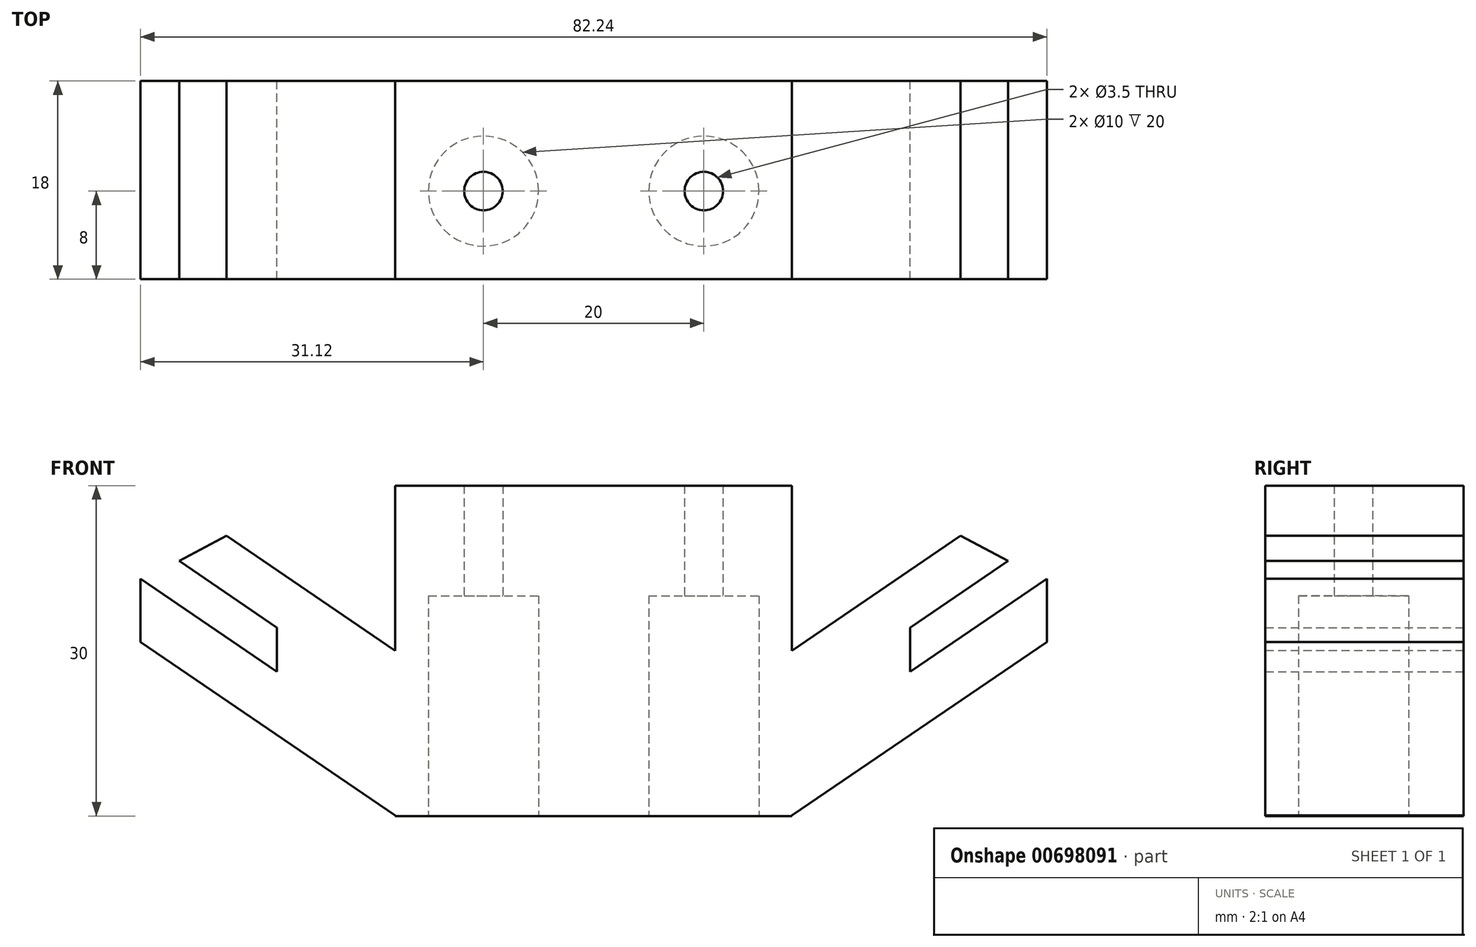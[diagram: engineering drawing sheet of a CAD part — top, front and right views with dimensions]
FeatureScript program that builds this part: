
annotation { "Feature Type Name" : "Feature", "Feature Type Description" : "" }
export const myFeature = defineFeature(function(context is Context, id is Id, definition is map)
    precondition{}
    {
        {
            var Q0;
            Q0=qCreatedBy(makeId("Top.planeOp"),FACE);
            var sketch = newSketch(context, id + "F0", { "sketchPlane" : qUnion([Q0])});
            skLineSegment(sketch, "E0.top", {"start": v(-10, -10) * mm, "end": v(10, -10) * mm, "construction": true});
            skPoint(sketch, "E0.middle", {"position": v(0, 0) * mm});
            skLineSegment(sketch, "E1.1", {"start": v(-18, 0) * mm, "end": v(-18, -18) * mm});
            skLineSegment(sketch, "E1.2", {"start": v(-18, -18) * mm, "end": v(18, -18) * mm});
            skLineSegment(sketch, "E1.3", {"start": v(18, 0) * mm, "end": v(18, -18) * mm});
            skLineSegment(sketch, "E2", {"start": v(-18, 0) * mm, "end": v(18, 0) * mm});
            skPoint(sketch, "E3.orphan", {"position": v(10, 10) * mm});
            skPoint(sketch, "E4.orphan", {"position": v(-10, 10) * mm});
            skPoint(sketch, "E1.0.end.orphan", {"position": v(18, 18) * mm});
            skPoint(sketch, "E1.0.start.orphan", {"position": v(-18, 18) * mm});
            skSolve(sketch);
        }
        {
            var Q0;
            Q0=makeQuery(id+"F0.imprint","IMPRINT",FACE,{"disambiguationData":[TD([[makeQuery(id+"F0.imprint","IMPRINT",EDGE,{"derivedFrom":sQuery(id+"F0.wireOp",EDGE,"E1.1")}),1.0]])]});
            extrude(context, id + "F1", {"entities" : qUnion([Q0]), "depth" : 15 * mm, "offsetDistance" : 25 * mm});
        }
        {
            var Q0;
            Q0=qCreatedBy(makeId("Front.planeOp"),FACE);
            var sketch = newSketch(context, id + "F2", { "sketchPlane" : qUnion([Q0])});
            skLineSegment(sketch, "E5", {"start": v(-18, 15) * mm, "end": v(-41.12, 30.79) * mm});
            skLineSegment(sketch, "E6", {"start": v(-41.12, 30.79) * mm, "end": v(-41.12, 25.56) * mm});
            skLineSegment(sketch, "E7", {"start": v(-41.12, 15.79) * mm, "end": v(-17.94, 0) * mm});
            skLineSegment(sketch, "E8", {"start": v(-41.12, 25.56) * mm, "end": v(-28.74, 17.1) * mm});
            skLineSegment(sketch, "E9", {"start": v(-28.74, 17.1) * mm, "end": v(-28.74, 13.1) * mm});
            skLineSegment(sketch, "E10", {"start": v(-28.74, 13.1) * mm, "end": v(-41.12, 21.56) * mm});
            skLineSegment(sketch, "E11.trimOffspring", {"start": v(-41.12, 21.56) * mm, "end": v(-41.12, 15.79) * mm});
            skLineSegment(sketch, "E12", {"start": v(-18, 15) * mm, "end": v(-17.94, 0) * mm});
            skLineSegment(sketch, "E13.MirrorCS", {"start": v(41.12, 25.56) * mm, "end": v(28.74, 17.1) * mm});
            skLineSegment(sketch, "E14.MirrorCS", {"start": v(28.74, 17.1) * mm, "end": v(28.74, 13.1) * mm});
            skLineSegment(sketch, "E15.MirrorCS", {"start": v(18, 15) * mm, "end": v(41.12, 30.79) * mm});
            skLineSegment(sketch, "E16.MirrorCS", {"start": v(28.74, 13.1) * mm, "end": v(41.12, 21.56) * mm});
            skLineSegment(sketch, "E17.MirrorCS", {"start": v(41.12, 15.79) * mm, "end": v(17.94, 0) * mm});
            skLineSegment(sketch, "E18.MirrorCS", {"start": v(41.12, 21.56) * mm, "end": v(41.12, 15.79) * mm});
            skLineSegment(sketch, "E19.MirrorCS", {"start": v(41.12, 30.79) * mm, "end": v(41.12, 25.56) * mm});
            skLineSegment(sketch, "E20.MirrorCS", {"start": v(18, 15) * mm, "end": v(17.94, 0) * mm});
            skSolve(sketch);
        }
        {
            var Q0;
            Q0=makeQuery(id+"F2.imprint","IMPRINT",FACE,{"disambiguationData":[TD([[makeQuery(id+"F2.imprint","IMPRINT",EDGE,{"derivedFrom":sQuery(id+"F2.wireOp",EDGE,"E5")}),1.0]])]});
            var Q1;
            Q1=makeQuery(id+"F2.imprint","IMPRINT",FACE,{"disambiguationData":[TD([[makeQuery(id+"F2.imprint","IMPRINT",EDGE,{"derivedFrom":sQuery(id+"F2.wireOp",EDGE,"E13.MirrorCS")}),-1.0]])]});
            extrude(context, id + "F3", {"entities" : qUnion([Q0, Q1]), "operationType" : NewBodyOperationType.ADD, "depth" : 18 * mm, "offsetDistance" : 25 * mm});
        }
        {
            var Q0;
            Q0=makeQuery(id+"F1.opExtrude","CAP_FACE",FACE,{"disambiguationData":[OSD([sQuery(id+"F0.wireOp",EDGE,"E1.1"),sQuery(id+"F0.wireOp",EDGE,"E1.2"),sQuery(id+"F0.wireOp",EDGE,"E1.3"),sQuery(id+"F0.wireOp",EDGE,"E2")])],"isStart":false});
            extrude(context, id + "F4", {"entities" : qUnion([Q0]), "operationType" : NewBodyOperationType.ADD, "depth" : 15 * mm, "offsetDistance" : 25 * mm});
        }
        {
            var Q0;
            Q0=makeQuery(id+"F3.opExtrude","SWEPT_EDGE",EDGE,{"disambiguationData":[OSD([sQuery(id+"F2.wireOp",EDGE,"E15.MirrorCS"),sQuery(id+"F2.wireOp",EDGE,"E19.MirrorCS")])]});
            var Q1;
            Q1=makeQuery(id+"F3.opExtrude","SWEPT_EDGE",EDGE,{"disambiguationData":[OSD([sQuery(id+"F2.wireOp",EDGE,"E5"),sQuery(id+"F2.wireOp",EDGE,"E6")])]});
            chamfer(context, id + "F5", {"entities" : qUnion([Q0, Q1]), "width" : 5 * mm, "tangentPropagation" : true});
        }
        {
            var Q0;
            Q0=sQuery(id+"F0.wireOp",VERTEX,"E0.left.end");
            var Q1;
            Q1=sQuery(id+"F0.wireOp",VERTEX,"E0.right.end");
            var Q2;
            Q2=sQuery(id+"F0.wireOp",VERTEX,"E0.top.start");
            var Q3;
            Q3=sQuery(id+"F0.wireOp",VERTEX,"E0.top.end");
            var Q4;
            Q4=makeQuery(id+"F1.opExtrude","SWEPT_BODY",BODY,{"disambiguationData":[OSD([sQuery(id+"F0.wireOp",EDGE,"E1.0"),sQuery(id+"F0.wireOp",EDGE,"E1.1"),sQuery(id+"F0.wireOp",EDGE,"E1.2"),sQuery(id+"F0.wireOp",EDGE,"E1.3")])]});
            hole(context, id + "F6", {"style" : HoleStyle.C_BORE, "endStyle" : HoleEndStyle.THROUGH, "oppositeDirection" : true, "holeDiameter" : 3.5 * mm, "cBoreDiameter" : 10 * mm, "cBoreDepth" : 20 * mm, "majorDiameter" : 5 * mm, "isTappedThrough" : true, "tappedDepth" : 12 * mm, "tapClearance" : 3, "startFromSketch" : true, "locations" : qUnion([Q0, Q1, Q2, Q3]), "scope" : qUnion([Q4])});
        }
    });
